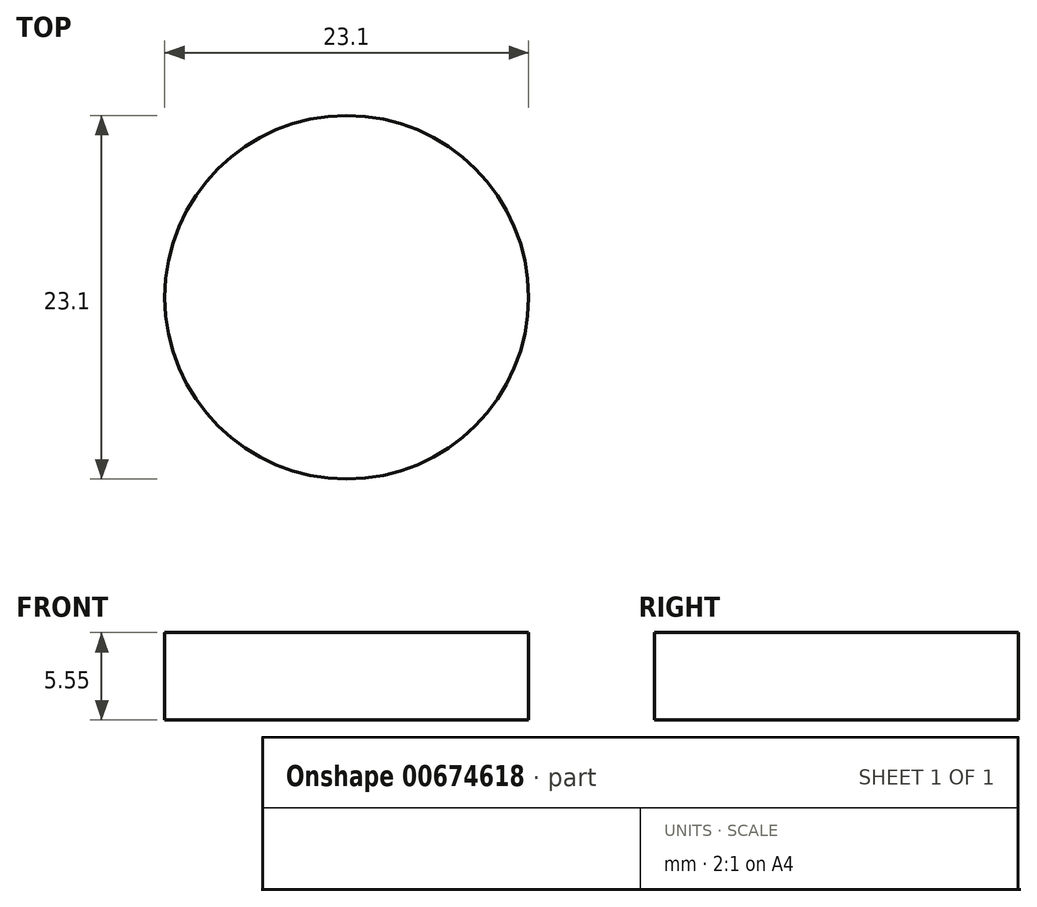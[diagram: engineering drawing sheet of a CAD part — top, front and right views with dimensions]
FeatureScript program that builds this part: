
annotation { "Feature Type Name" : "Feature", "Feature Type Description" : "" }
export const myFeature = defineFeature(function(context is Context, id is Id, definition is map)
    precondition{}
    {
        {
            var Q0;
            Q0=qCreatedBy(makeId("Top.planeOp"),FACE);
            var sketch = newSketch(context, id + "F0", { "sketchPlane" : qUnion([Q0])});
            skCircle(sketch, "E0", {"center": v(0, 11.55) * mm, "radius": 11.55 * mm});
            skSolve(sketch);
        }
        {
            var Q0;
            Q0=makeQuery(id+"F0.imprint","IMPRINT",FACE,{"disambiguationData":[TD([[makeQuery(id+"F0.imprint","IMPRINT",EDGE,{"derivedFrom":sQuery(id+"F0.wireOp",EDGE,"E0")}),1.0]])]});
            extrude(context, id + "F1", {"entities" : qUnion([Q0]), "depth" : 5.55 * mm, "offsetDistance" : 25 * mm});
        }
    });
